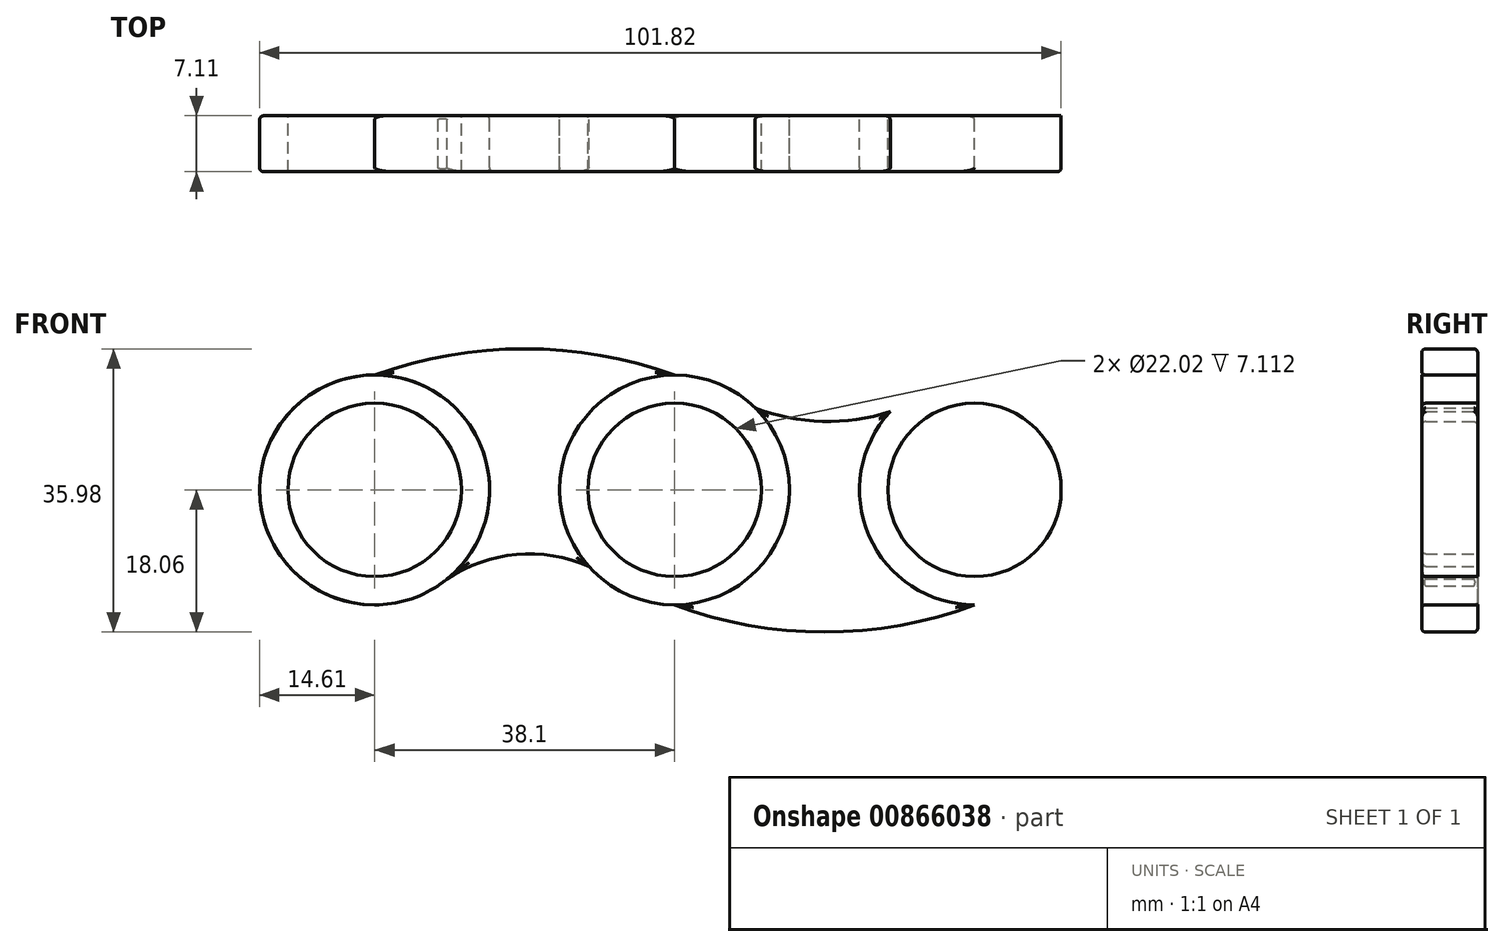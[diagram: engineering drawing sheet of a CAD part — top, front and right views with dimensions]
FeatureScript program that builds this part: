
annotation { "Feature Type Name" : "Feature", "Feature Type Description" : "" }
export const myFeature = defineFeature(function(context is Context, id is Id, definition is map)
    precondition{}
    {
        {
            var Q0;
            Q0=qCreatedBy(makeId("Front.planeOp"),FACE);
            var sketch = newSketch(context, id + "F0", { "sketchPlane" : qUnion([Q0])});
            skCircle(sketch, "E0", {"center": v(0, 0) * mm, "radius": 11.01 * mm});
            skCircle(sketch, "E1", {"center": v(0, 0) * mm, "radius": 14.6 * mm});
            skLineSegment(sketch, "E2", {"start": v(-38.1, 22.23) * mm, "end": v(-38.1, -24.16) * mm, "construction": true});
            skCircle(sketch, "E3", {"center": v(-38.1, 0) * mm, "radius": 11.01 * mm});
            skCircle(sketch, "E4", {"center": v(-38.1, 0) * mm, "radius": 14.6 * mm});
            skArc(sketch, "E5", {"start": v(0, 14.6) * mm, "mid": v(-19.05, 17.92) * mm, "end": v(-38.1, 14.6) * mm});
            skArc(sketch, "E6", {"start": v(-10.89, -9.73) * mm, "mid": v(-20.81, -8.28) * mm, "end": v(-30.05, -12.19) * mm});
            skCircle(sketch, "E7.MirrorC", {"center": v(38.1, 0) * mm, "radius": 14.6 * mm});
            skCircle(sketch, "E8.MirrorC", {"center": v(38.1, 0) * mm, "radius": 11.01 * mm});
            skArc(sketch, "E9", {"start": v(10.22, 10.43) * mm, "mid": v(18.77, 8.7) * mm, "end": v(27.4, 9.94) * mm});
            skLineSegment(sketch, "E10.MirrorCS", {"start": v(38.1, 22.23) * mm, "end": v(38.1, -24.16) * mm, "construction": true});
            skArc(sketch, "E11", {"start": v(0, -14.6) * mm, "mid": v(19.05, -18.06) * mm, "end": v(38.1, -14.6) * mm});
            skSolve(sketch);
        }
        {
            var Q0;
            Q0=makeQuery(id+"F0.imprint","IMPRINT",FACE,{"disambiguationData":[TD([[makeQuery(id+"F0.imprint","IMPRINT",EDGE,{"derivedFrom":sQuery(id+"F0.wireOp",EDGE,"E8.MirrorC")}),1.0]])]});
            var Q1;
            Q1=makeQuery(id+"F0.imprint","IMPRINT",FACE,{"disambiguationData":[TD([[makeQuery(id+"F0.imprint","IMPRINT",EDGE,{"derivedFrom":sQuery(id+"F0.wireOp",EDGE,"E0")}),-1.0]])]});
            var Q2;
            Q2=makeQuery(id+"F0.imprint","IMPRINT",FACE,{"disambiguationData":[TD([[makeQuery(id+"F0.imprint","IMPRINT",EDGE,{"derivedFrom":sQuery(id+"F0.wireOp",EDGE,"E3")}),-1.0]])]});
            extrude(context, id + "F1", {"entities" : qUnion([Q0, Q1, Q2]), "depth" : 7.11 * mm, "offsetDistance" : 25.4 * mm});
        }
        {
            var Q0;
            {var subQ0=sQuery(id+"F0.wireOp",EDGE,"E5");Q0=makeQuery(id+"F0.imprint","IMPRINT",FACE,{"disambiguationData":[TD([[makeQuery(id+"F0.imprint","IMPRINT",EDGE,{"derivedFrom":subQ0}),1.0]])]});}
            var Q1;
            {var subQ0=sQuery(id+"F0.wireOp",EDGE,"E9");Q1=makeQuery(id+"F0.imprint","IMPRINT",FACE,{"disambiguationData":[TD([[makeQuery(id+"F0.imprint","IMPRINT",EDGE,{"derivedFrom":subQ0}),-1.0]])]});}
            extrude(context, id + "F2", {"entities" : qUnion([Q0, Q1]), "depth" : 7.11 * mm, "offsetDistance" : 25.4 * mm});
        }
        {
            var Q0;
            Q0=makeQuery(id+"F1.opExtrude","CAP_EDGE",EDGE,{"disambiguationData":[OSD([sQuery(id+"F0.wireOp",EDGE,"E4")])],"isStart":false});
            var Q1;
            Q1=makeQuery(id+"F2.opExtrude","CAP_FACE",FACE,{"disambiguationData":[OSD([sQuery(id+"F0.wireOp",EDGE,"E4"),sQuery(id+"F0.wireOp",EDGE,"E5"),sQuery(id+"F0.wireOp",EDGE,"137f216a-2c94-4fd5-a3a7-790f7f5d5f550.MirrorCS"),sQuery(id+"F0.wireOp",EDGE,"E1")])],"isStart":false});
            var Q2;
            Q2=makeQuery(id+"F1.opExtrude","CAP_EDGE",EDGE,{"disambiguationData":[OSD([sQuery(id+"F0.wireOp",EDGE,"E1")])],"isStart":false});
            var Q3;
            Q3=makeQuery(id+"F2.opExtrude","CAP_FACE",FACE,{"disambiguationData":[OSD([sQuery(id+"F0.wireOp",EDGE,"E7.MirrorC"),sQuery(id+"F0.wireOp",EDGE,"E1"),sQuery(id+"F0.wireOp",EDGE,"E9"),sQuery(id+"F0.wireOp",EDGE,"E11")])],"isStart":false});
            var Q4;
            Q4=makeQuery(id+"F1.opExtrude","CAP_FACE",FACE,{"disambiguationData":[OSD([sQuery(id+"F0.wireOp",EDGE,"E7.MirrorC"),sQuery(id+"F0.wireOp",EDGE,"E8.MirrorC")])],"isStart":false});
            var Q5;
            Q5=makeQuery(id+"F2.opExtrude","CAP_EDGE",EDGE,{"disambiguationData":[OSD([sQuery(id+"F0.wireOp",EDGE,"E11")])],"isStart":true});
            var Q6;
            Q6=makeQuery(id+"F2.opExtrude","CAP_EDGE",EDGE,{"disambiguationData":[OSD([sQuery(id+"F0.wireOp",EDGE,"E9")])],"isStart":true});
            var Q7;
            Q7=makeQuery(id+"F1.opExtrude","CAP_EDGE",EDGE,{"disambiguationData":[OSD([sQuery(id+"F0.wireOp",EDGE,"E7.MirrorC")])],"isStart":true});
            var Q8;
            Q8=makeQuery(id+"F1.opExtrude","CAP_EDGE",EDGE,{"disambiguationData":[OSD([sQuery(id+"F0.wireOp",EDGE,"E1")])],"isStart":true});
            var Q9;
            Q9=makeQuery(id+"F2.opExtrude","CAP_EDGE",EDGE,{"disambiguationData":[OSD([sQuery(id+"F0.wireOp",EDGE,"137f216a-2c94-4fd5-a3a7-790f7f5d5f550.MirrorCS")])],"isStart":true});
            var Q10;
            Q10=makeQuery(id+"F2.opExtrude","CAP_EDGE",EDGE,{"disambiguationData":[OSD([sQuery(id+"F0.wireOp",EDGE,"E5")])],"isStart":true});
            var Q11;
            Q11=makeQuery(id+"F1.opExtrude","CAP_EDGE",EDGE,{"disambiguationData":[OSD([sQuery(id+"F0.wireOp",EDGE,"E4")])],"isStart":true});
            var Q12;
            Q12=makeQuery(id+"F2.opExtrude","CAP_EDGE",EDGE,{"disambiguationData":[OSD([sQuery(id+"F0.wireOp",EDGE,"E7.MirrorC")])],"isStart":false});
            var Q13;
            Q13=makeQuery(id+"F1.opExtrude","CAP_EDGE",EDGE,{"disambiguationData":[OSD([sQuery(id+"F0.wireOp",EDGE,"E7.MirrorC")])],"isStart":false});
            fillet(context, id + "F3", {"entities" : qUnion([Q0, Q1, Q2, Q3, Q4, Q5, Q6, Q7, Q8, Q9, Q10, Q11, Q12, Q13]), "radius" : 0.5 * mm, "tangentPropagation" : true, "allowEdgeOverflow" : false});
        }
    });
